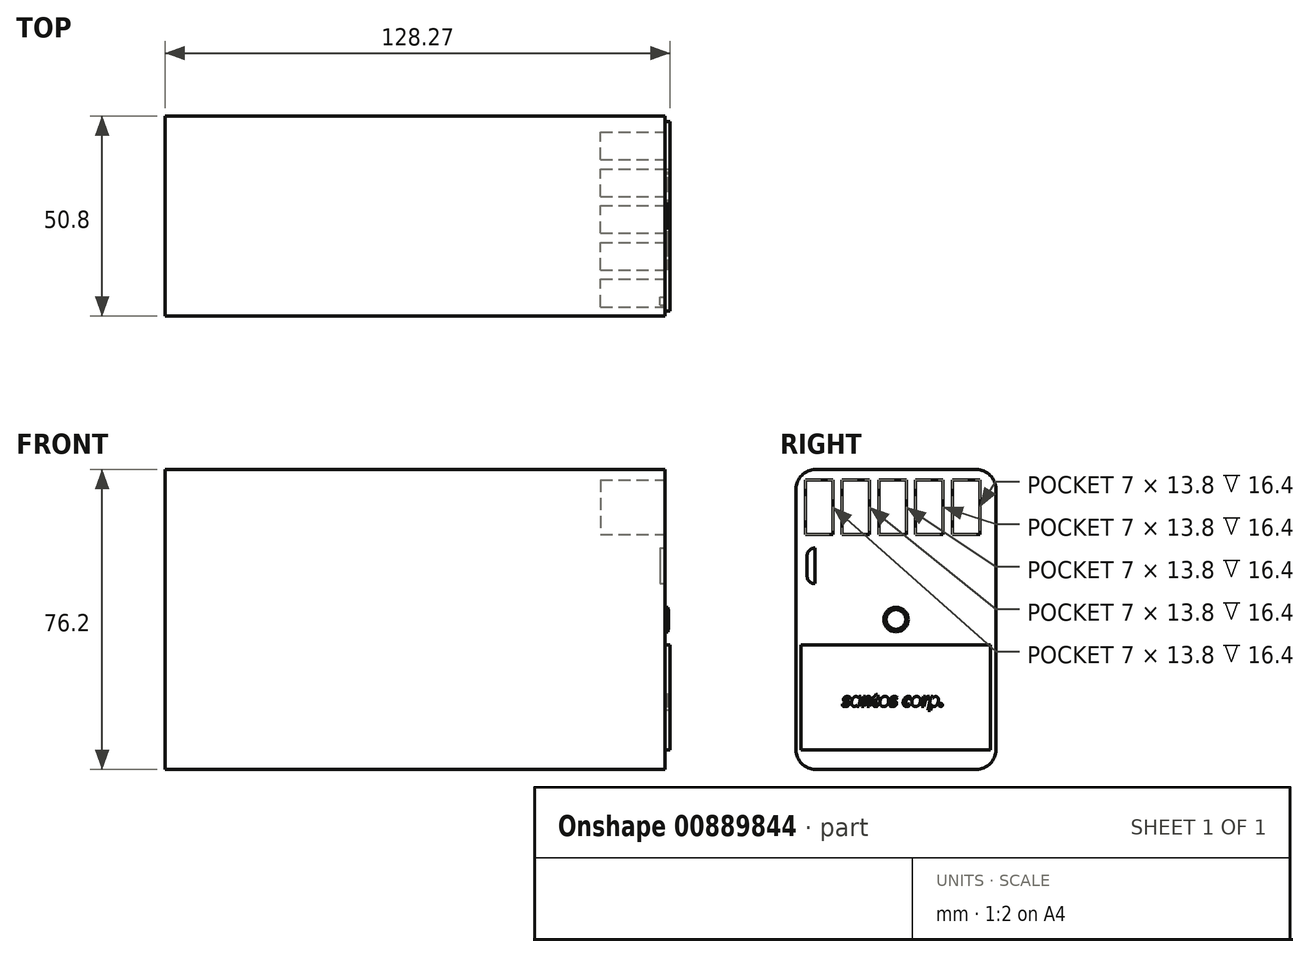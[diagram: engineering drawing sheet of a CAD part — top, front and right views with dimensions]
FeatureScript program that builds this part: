
annotation { "Feature Type Name" : "Feature", "Feature Type Description" : "" }
export const myFeature = defineFeature(function(context is Context, id is Id, definition is map)
    precondition{}
    {
        {
            var Q0;
            Q0=qCreatedBy(makeId("Front.planeOp"),FACE);
            var sketch = newSketch(context, id + "F0", { "sketchPlane" : qUnion([Q0])});
            skLineSegment(sketch, "E0.bottom", {"start": v(63.5, -38.1) * mm, "end": v(-63.5, -38.1) * mm});
            skLineSegment(sketch, "E0.top", {"start": v(63.5, 38.1) * mm, "end": v(-63.5, 38.1) * mm});
            skLineSegment(sketch, "E0.left", {"start": v(63.5, -38.1) * mm, "end": v(63.5, 38.1) * mm});
            skLineSegment(sketch, "E0.right", {"start": v(-63.5, -38.1) * mm, "end": v(-63.5, 38.1) * mm});
            skPoint(sketch, "E0.middle", {"position": v(0, 0) * mm});
            skSolve(sketch);
        }
        {
            var Q0;
            Q0=makeQuery(id+"F0.imprint","IMPRINT",FACE,{"disambiguationData":[TD([[makeQuery(id+"F0.imprint","IMPRINT",EDGE,{"derivedFrom":sQuery(id+"F0.wireOp",EDGE,"E0.bottom")}),-1.0]])]});
            extrude(context, id + "F1", {"entities" : qUnion([Q0]), "depth" : 50.8 * mm, "offsetDistance" : 25.4 * mm, "symmetric" : true});
        }
        {
            var Q0;
            Q0=makeQuery(id+"F1.opExtrude","CAP_EDGE",EDGE,{"disambiguationData":[OSD([sQuery(id+"F0.wireOp",EDGE,"E0.top")])],"isStart":false});
            var Q1;
            Q1=makeQuery(id+"F1.opExtrude","CAP_EDGE",EDGE,{"disambiguationData":[OSD([sQuery(id+"F0.wireOp",EDGE,"E0.top")])],"isStart":true});
            var Q2;
            Q2=makeQuery(id+"F1.opExtrude","CAP_EDGE",EDGE,{"disambiguationData":[OSD([sQuery(id+"F0.wireOp",EDGE,"E0.bottom")])],"isStart":true});
            var Q3;
            Q3=makeQuery(id+"F1.opExtrude","CAP_EDGE",EDGE,{"disambiguationData":[OSD([sQuery(id+"F0.wireOp",EDGE,"E0.bottom")])],"isStart":false});
            fillet(context, id + "F2", {"entities" : qUnion([Q0, Q1, Q2, Q3]), "radius" : 5 * mm, "tangentPropagation" : true, "allowEdgeOverflow" : false});
        }
        {
            var Q0;
            Q0=makeQuery(id+"F1.opExtrude","SWEPT_FACE",FACE,{"disambiguationData":[OSD([sQuery(id+"F0.wireOp",EDGE,"E0.left")])]});
            var sketch = newSketch(context, id + "F3", { "sketchPlane" : qUnion([Q0])});
            skLineSegment(sketch, "E1.bottom", {"start": v(-23.05, 35.44) * mm, "end": v(-16.05, 35.44) * mm});
            skLineSegment(sketch, "E1.top", {"start": v(-23.05, 21.64) * mm, "end": v(-16.05, 21.64) * mm});
            skLineSegment(sketch, "E1.left", {"start": v(-23.05, 35.44) * mm, "end": v(-23.05, 21.64) * mm});
            skLineSegment(sketch, "E1.right", {"start": v(-16.05, 35.44) * mm, "end": v(-16.05, 21.64) * mm});
            skLineSegment(sketch, "E2.bottom", {"start": v(-25.4, 21.64) * mm, "end": v(-23.05, 21.64) * mm});
            skLineSegment(sketch, "E2.top", {"start": v(-25.4, 21.64) * mm, "end": v(-23.05, 21.64) * mm});
            skLineSegment(sketch, "E2.left", {"start": v(-25.4, 21.64) * mm, "end": v(-25.4, 21.64) * mm});
            skLineSegment(sketch, "E2.right", {"start": v(-23.05, 21.64) * mm, "end": v(-23.05, 21.64) * mm});
            skLineSegment(sketch, "E3.top", {"start": v(-16.05, 21.64) * mm, "end": v(-13.7, 21.64) * mm});
            skLineSegment(sketch, "E4.bottom", {"start": v(-13.7, 35.44) * mm, "end": v(-6.7, 35.44) * mm});
            skLineSegment(sketch, "E4.top", {"start": v(-13.7, 21.64) * mm, "end": v(-6.7, 21.64) * mm});
            skLineSegment(sketch, "E4.left", {"start": v(-13.7, 35.44) * mm, "end": v(-13.7, 21.64) * mm});
            skLineSegment(sketch, "E4.right", {"start": v(-6.7, 35.44) * mm, "end": v(-6.7, 21.64) * mm});
            skLineSegment(sketch, "E5.top", {"start": v(-6.7, 21.64) * mm, "end": v(-4.36, 21.64) * mm});
            skLineSegment(sketch, "E6.bottom", {"start": v(-4.36, 35.44) * mm, "end": v(2.64, 35.44) * mm});
            skLineSegment(sketch, "E6.top", {"start": v(-4.36, 21.64) * mm, "end": v(2.64, 21.64) * mm});
            skLineSegment(sketch, "E6.left", {"start": v(-4.36, 35.44) * mm, "end": v(-4.36, 21.64) * mm});
            skLineSegment(sketch, "E6.right", {"start": v(2.64, 35.44) * mm, "end": v(2.64, 21.64) * mm});
            skLineSegment(sketch, "E7.top", {"start": v(2.64, 21.64) * mm, "end": v(4.99, 21.64) * mm});
            skLineSegment(sketch, "E8.bottom", {"start": v(4.99, 35.44) * mm, "end": v(11.99, 35.44) * mm});
            skLineSegment(sketch, "E8.top", {"start": v(4.99, 21.64) * mm, "end": v(11.99, 21.64) * mm});
            skLineSegment(sketch, "E8.left", {"start": v(4.99, 35.44) * mm, "end": v(4.99, 21.64) * mm});
            skLineSegment(sketch, "E8.right", {"start": v(11.99, 35.44) * mm, "end": v(11.99, 21.64) * mm});
            skLineSegment(sketch, "E9.top", {"start": v(11.99, 21.64) * mm, "end": v(14.33, 21.64) * mm});
            skLineSegment(sketch, "E10.bottom", {"start": v(14.33, 35.44) * mm, "end": v(21.33, 35.44) * mm});
            skLineSegment(sketch, "E10.top", {"start": v(14.33, 21.64) * mm, "end": v(21.33, 21.64) * mm});
            skLineSegment(sketch, "E10.left", {"start": v(14.33, 35.44) * mm, "end": v(14.33, 21.64) * mm});
            skLineSegment(sketch, "E10.right", {"start": v(21.33, 35.44) * mm, "end": v(21.33, 21.64) * mm});
            skSolve(sketch);
        }
        {
            var Q0;
            Q0 = qSketchRegion(id + "F3", true);
            extrude(context, id + "F4", {"entities" : qUnion([Q0]), "operationType" : NewBodyOperationType.REMOVE, "oppositeDirection" : true, "depth" : 16.4 * mm, "offsetDistance" : 25.4 * mm});
        }
        {
            var Q0;
            Q0=makeQuery(id+"F1.opExtrude","SWEPT_FACE",FACE,{"disambiguationData":[OSD([sQuery(id+"F0.wireOp",EDGE,"E0.left")])]});
            var sketch = newSketch(context, id + "F5", { "sketchPlane" : qUnion([Q0])});
            skCircle(sketch, "E11", {"center": v(0, 0) * mm, "radius": 2.5 * mm});
            skSolve(sketch);
        }
        {
            var Q0;
            Q0=makeQuery(id+"F5.imprint","IMPRINT",FACE,{"disambiguationData":[TD([[makeQuery(id+"F5.imprint","IMPRINT",EDGE,{"derivedFrom":sQuery(id+"F5.wireOp",EDGE,"E11")}),-1.0]])]});
            var sketch = newSketch(context, id + "F6", { "sketchPlane" : qUnion([Q0])});
            skCircle(sketch, "E12", {"center": v(0, 0) * mm, "radius": 3.1 * mm});
            skSolve(sketch);
        }
        {
            var Q0;
            Q0 = qSketchRegion(id + "F5", true);
            extrude(context, id + "F7", {"entities" : qUnion([Q0]), "operationType" : NewBodyOperationType.ADD, "depth" : 0.89 * mm, "offsetDistance" : 25.4 * mm});
        }
        {
            var Q0;
            Q0 = qSketchRegion(id + "F6", true);
            extrude(context, id + "F8", {"entities" : qUnion([Q0]), "operationType" : NewBodyOperationType.ADD, "depth" : 0.76 * mm, "offsetDistance" : 25.4 * mm});
        }
        {
            var Q0;
            Q0=makeQuery(id+"F1.opExtrude","SWEPT_FACE",FACE,{"disambiguationData":[OSD([sQuery(id+"F0.wireOp",EDGE,"E0.left")])]});
            var sketch = newSketch(context, id + "F9", { "sketchPlane" : qUnion([Q0])});
            skLineSegment(sketch, "E13.bottom", {"start": v(-22.57, 18.13) * mm, "end": v(-20.54, 18.13) * mm});
            skLineSegment(sketch, "E13.top", {"start": v(-22.57, 9.1) * mm, "end": v(-20.54, 9.1) * mm});
            skLineSegment(sketch, "E13.left", {"start": v(-22.57, 18.13) * mm, "end": v(-22.57, 9.1) * mm});
            skLineSegment(sketch, "E13.right", {"start": v(-20.54, 18.13) * mm, "end": v(-20.54, 9.1) * mm});
            skSolve(sketch);
        }
        {
            var Q0;
            Q0=makeQuery(id+"F9.imprint","IMPRINT",FACE,{"disambiguationData":[TD([[makeQuery(id+"F9.imprint","IMPRINT",EDGE,{"derivedFrom":sQuery(id+"F9.wireOp",EDGE,"E13.bottom")}),-1.0]])]});
            extrude(context, id + "F10", {"entities" : qUnion([Q0]), "operationType" : NewBodyOperationType.REMOVE, "oppositeDirection" : true, "depth" : 1.27 * mm, "offsetDistance" : 25.4 * mm});
        }
        {
            var Q0;
            Q0=makeQuery(id+"F10.boolean.opBoolean","COPY",EDGE,{"derivedFrom":makeQuery(id+"F10.opExtrude","SWEPT_EDGE",EDGE,{"disambiguationData":[OSD([sQuery(id+"F9.wireOp",EDGE,"E13.bottom"),sQuery(id+"F9.wireOp",EDGE,"E13.left")])]})});
            var Q1;
            Q1=makeQuery(id+"F10.boolean.opBoolean","COPY",EDGE,{"derivedFrom":makeQuery(id+"F10.opExtrude","SWEPT_EDGE",EDGE,{"disambiguationData":[OSD([sQuery(id+"F9.wireOp",EDGE,"E13.top"),sQuery(id+"F9.wireOp",EDGE,"E13.left")])]})});
            fillet(context, id + "F11", {"entities" : qUnion([Q0, Q1]), "radius" : 1.9 * mm, "tangentPropagation" : true, "allowEdgeOverflow" : false});
        }
        {
            var Q0;
            Q0=makeQuery(id+"F1.opExtrude","SWEPT_FACE",FACE,{"disambiguationData":[OSD([sQuery(id+"F0.wireOp",EDGE,"E0.left")])]});
            var sketch = newSketch(context, id + "F12", { "sketchPlane" : qUnion([Q0])});
            skLineSegment(sketch, "E14.bottom", {"start": v(-24.14, -6.51) * mm, "end": v(23.95, -6.51) * mm});
            skLineSegment(sketch, "E14.top", {"start": v(-24.14, -33.1) * mm, "end": v(23.95, -33.1) * mm});
            skLineSegment(sketch, "E14.left", {"start": v(-24.14, -6.51) * mm, "end": v(-24.14, -33.1) * mm});
            skLineSegment(sketch, "E14.right", {"start": v(23.95, -6.51) * mm, "end": v(23.95, -33.1) * mm});
            skPoint(sketch, "E15", {"position": v(5.9, 13.38) * mm});
            skPoint(sketch, "E16", {"position": v(12.36, 10.17) * mm});
            skPoint(sketch, "E17", {"position": v(16.3, 13.38) * mm});
            skText(sketch, "E18", { "text": "santos corp.\n", "fontName": "OpenSans-BoldItalic.ttf"});
            const initialGuessF12  = {"E18": [-0.01362, -0.02206, 1, 0, 0.00323]};
            skSetInitialGuess(sketch, initialGuessF12);
            skSolve(sketch);
        }
        {
            var Q0;
            Q0 = qSketchRegion(id + "F12", true);
            extrude(context, id + "F13", {"entities" : qUnion([Q0]), "operationType" : NewBodyOperationType.ADD, "depth" : 1.27 * mm, "offsetDistance" : 25.4 * mm});
        }
    });
